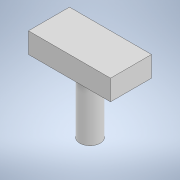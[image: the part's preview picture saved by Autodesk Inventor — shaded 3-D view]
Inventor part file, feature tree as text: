
AUTODESK INVENTOR PART (.ipt)
format: ipt  version: 2021 (Build 250183000, 183)  size: 98,816 bytes
history: native  units: in
note: dims shown in document units (in); Inventor stores cm internally (conversion verified against a paired STEP export)
features: extrude x2, sketch x2
ambient origin geometry x8: Origin, YZ Plane, XZ Plane, XY Plane, X Axis, Y Axis, Z Axis, Center Point
bodies: Solid1 (feature_tree)
feature tree (4):
  extrude  "Extrusion1"  Depth=4.0in
  extrude  "Extrusion2"  Depth=1.0in
  sketch  "Sketch1"  dims[d0=2.0in d1=4.0in]
  sketch  "Sketch2"  dims[d2=1.0in d3=0.0in d4=1.0in d5=3.0in d6=0.0in]
